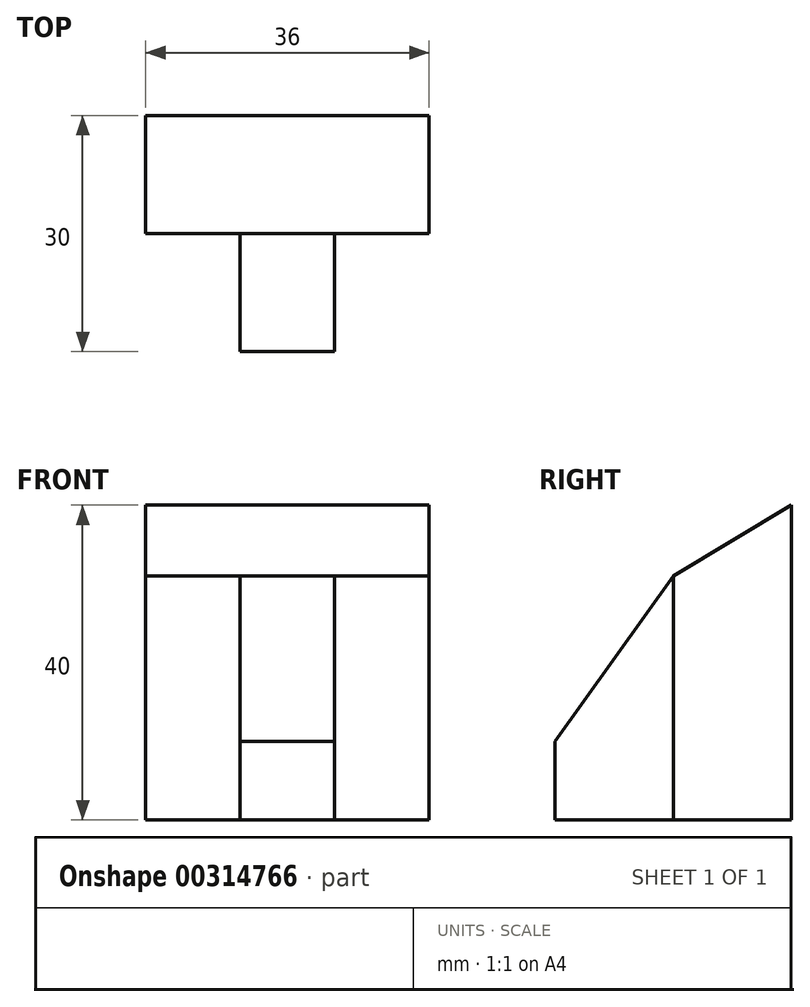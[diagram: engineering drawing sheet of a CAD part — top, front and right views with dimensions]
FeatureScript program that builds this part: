
annotation { "Feature Type Name" : "Feature", "Feature Type Description" : "" }
export const myFeature = defineFeature(function(context is Context, id is Id, definition is map)
    precondition{}
    {
        {
            var Q0;
            Q0=qCreatedBy(makeId("Right.planeOp"),FACE);
            var sketch = newSketch(context, id + "F0", { "sketchPlane" : qUnion([Q0])});
            skLineSegment(sketch, "E0.bottom", {"start": v(0, 0) * mm, "end": v(30, 0) * mm});
            skLineSegment(sketch, "E0.top", {"start": v(0, 40) * mm, "end": v(30, 40) * mm});
            skLineSegment(sketch, "E0.left", {"start": v(0, 0) * mm, "end": v(0, 40) * mm});
            skLineSegment(sketch, "E0.right", {"start": v(30, 0) * mm, "end": v(30, 40) * mm});
            skLineSegment(sketch, "E1", {"start": v(30, 40) * mm, "end": v(0, 22) * mm});
            skLineSegment(sketch, "E2", {"start": v(15, 0) * mm, "end": v(15, 31) * mm});
            skLineSegment(sketch, "E3", {"start": v(15, 31) * mm, "end": v(0, 10) * mm});
            skSolve(sketch);
        }
        {
            var Q0;
            {var subQ0=sQuery(id+"F0.wireOp",EDGE,"E0.right");Q0=makeQuery(id+"F0.imprint","IMPRINT",FACE,{"disambiguationData":[TD([[makeQuery(id+"F0.imprint","IMPRINT",EDGE,{"derivedFrom":subQ0}),1.0]])]});}
            extrude(context, id + "F1", {"entities" : qUnion([Q0]), "depth" : 36 * mm, "symmetric" : true});
        }
        {
            var Q0;
            {var subQ3=sQuery(id+"F0.wireOp",EDGE,"E2");Q0=makeQuery(id+"F0.imprint","IMPRINT",FACE,{"disambiguationData":[TD([[makeQuery(id+"F0.imprint","IMPRINT",EDGE,{"derivedFrom":subQ3}),1.0]])]});}
            extrude(context, id + "F2", {"entities" : qUnion([Q0]), "operationType" : NewBodyOperationType.ADD, "depth" : 12 * mm, "symmetric" : true});
        }
    });
